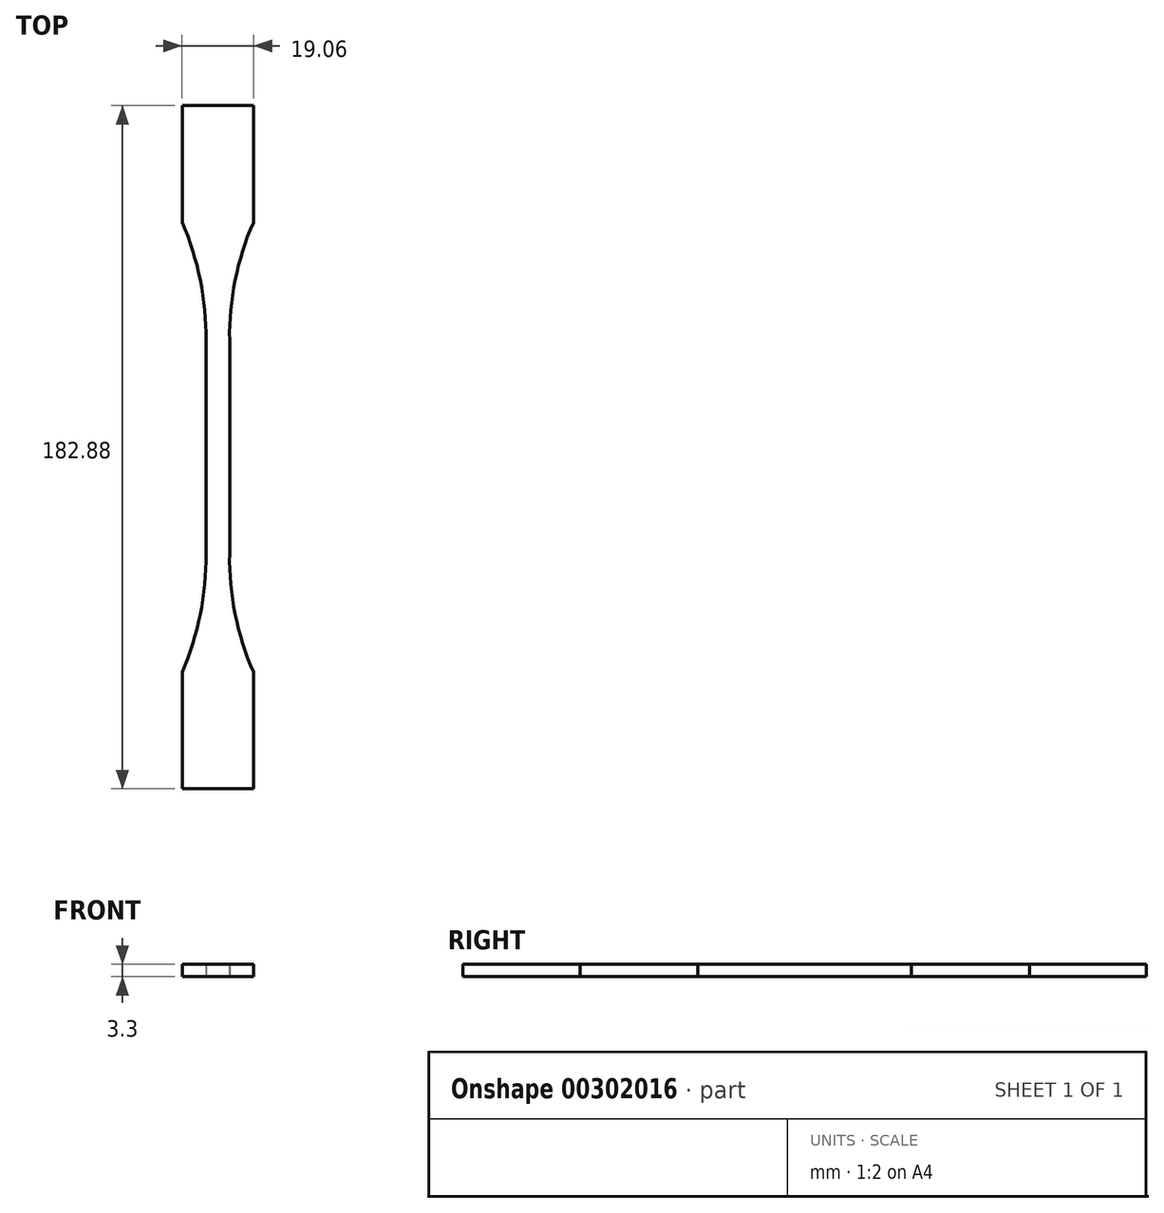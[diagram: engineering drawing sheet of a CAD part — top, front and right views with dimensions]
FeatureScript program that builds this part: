
annotation { "Feature Type Name" : "Feature", "Feature Type Description" : "" }
export const myFeature = defineFeature(function(context is Context, id is Id, definition is map)
    precondition{}
    {
        {
            var Q0;
            Q0=qCreatedBy(makeId("Top.planeOp"),FACE);
            var sketch = newSketch(context, id + "F0", { "sketchPlane" : qUnion([Q0])});
            skLineSegment(sketch, "E0", {"start": v(-3.17, 0) * mm, "end": v(-3.17, 28.58) * mm});
            skLineSegment(sketch, "E1", {"start": v(-9.53, 60.12) * mm, "end": v(-9.53, 91.44) * mm});
            skLineSegment(sketch, "E2", {"start": v(-9.53, 91.44) * mm, "end": v(0, 91.44) * mm});
            skArc(sketch, "E3", {"start": v(-3.17, 28.57) * mm, "mid": v(-4.67, 44.69) * mm, "end": v(-9.52, 60.12) * mm});
            skArc(sketch, "E4.MirrorCS", {"start": v(3.17, 28.57) * mm, "mid": v(4.67, 44.69) * mm, "end": v(9.52, 60.12) * mm});
            skLineSegment(sketch, "E5.MirrorCS", {"start": v(9.52, 60.12) * mm, "end": v(9.52, 91.44) * mm});
            skLineSegment(sketch, "E6.MirrorCS", {"start": v(9.52, 91.44) * mm, "end": v(0, 91.44) * mm});
            skLineSegment(sketch, "E7.MirrorCS", {"start": v(3.17, 0) * mm, "end": v(3.17, 28.58) * mm});
            skLineSegment(sketch, "E8", {"start": v(-3.17, 0) * mm, "end": v(3.17, 0) * mm, "construction": true});
            skLineSegment(sketch, "E9.MirrorCS", {"start": v(3.17, 0) * mm, "end": v(3.17, -28.58) * mm});
            skLineSegment(sketch, "E10.MirrorCS", {"start": v(9.52, -91.44) * mm, "end": v(0, -91.44) * mm});
            skLineSegment(sketch, "E11.MirrorCS", {"start": v(9.52, -60.12) * mm, "end": v(9.52, -91.44) * mm});
            skLineSegment(sketch, "E12.MirrorCS", {"start": v(-9.53, -60.12) * mm, "end": v(-9.53, -91.44) * mm});
            skLineSegment(sketch, "E13.MirrorCS", {"start": v(-9.53, -91.44) * mm, "end": v(0, -91.44) * mm});
            skLineSegment(sketch, "E14.MirrorCS", {"start": v(-3.17, 0) * mm, "end": v(-3.17, -28.58) * mm});
            skArc(sketch, "E15.MirrorCS", {"start": v(-3.17, -28.57) * mm, "mid": v(-4.67, -44.69) * mm, "end": v(-9.52, -60.12) * mm});
            skArc(sketch, "E16.MirrorCS", {"start": v(3.17, -28.57) * mm, "mid": v(4.67, -44.69) * mm, "end": v(9.52, -60.12) * mm});
            skSolve(sketch);
        }
        {
            var Q0;
            Q0=makeQuery(id+"F0.imprint","IMPRINT",FACE,{"disambiguationData":[TD([[makeQuery(id+"F0.imprint","IMPRINT",EDGE,{"derivedFrom":sQuery(id+"F0.wireOp",EDGE,"E0")}),-1.0]])]});
            var Q1;
            Q1=sQuery(id+"F0.wireOp",EDGE,"E14.MirrorCS");
            var Q2;
            Q2=sQuery(id+"F0.wireOp",EDGE,"E3");
            var Q3;
            Q3=sQuery(id+"F0.wireOp",EDGE,"E15.MirrorCS");
            var Q4;
            Q4=sQuery(id+"F0.wireOp",EDGE,"E2");
            var Q5;
            Q5=sQuery(id+"F0.wireOp",EDGE,"E0");
            var Q6;
            Q6=sQuery(id+"F0.wireOp",EDGE,"E1");
            var Q7;
            Q7=sQuery(id+"F0.wireOp",EDGE,"E13.MirrorCS");
            var Q8;
            Q8=sQuery(id+"F0.wireOp",EDGE,"E4.MirrorCS");
            var Q9;
            Q9=sQuery(id+"F0.wireOp",EDGE,"E5.MirrorCS");
            var Q10;
            Q10=sQuery(id+"F0.wireOp",EDGE,"E7.MirrorCS");
            var Q11;
            Q11=sQuery(id+"F0.wireOp",EDGE,"E9.MirrorCS");
            var Q12;
            Q12=sQuery(id+"F0.wireOp",EDGE,"E11.MirrorCS");
            var Q13;
            Q13=sQuery(id+"F0.wireOp",EDGE,"E12.MirrorCS");
            var Q14;
            Q14=sQuery(id+"F0.wireOp",EDGE,"E16.MirrorCS");
            var Q15;
            Q15=sQuery(id+"F0.wireOp",EDGE,"E6.MirrorCS");
            var Q16;
            Q16=sQuery(id+"F0.wireOp",EDGE,"E10.MirrorCS");
            extrude(context, id + "F1", {"entities" : qUnion([Q0]), "surfaceEntities" : qUnion([Q1, Q2, Q3, Q4, Q5, Q6, Q7, Q8, Q9, Q10, Q11, Q12, Q13, Q14, Q15, Q16]), "depth" : 3.3 * mm});
        }
    });
